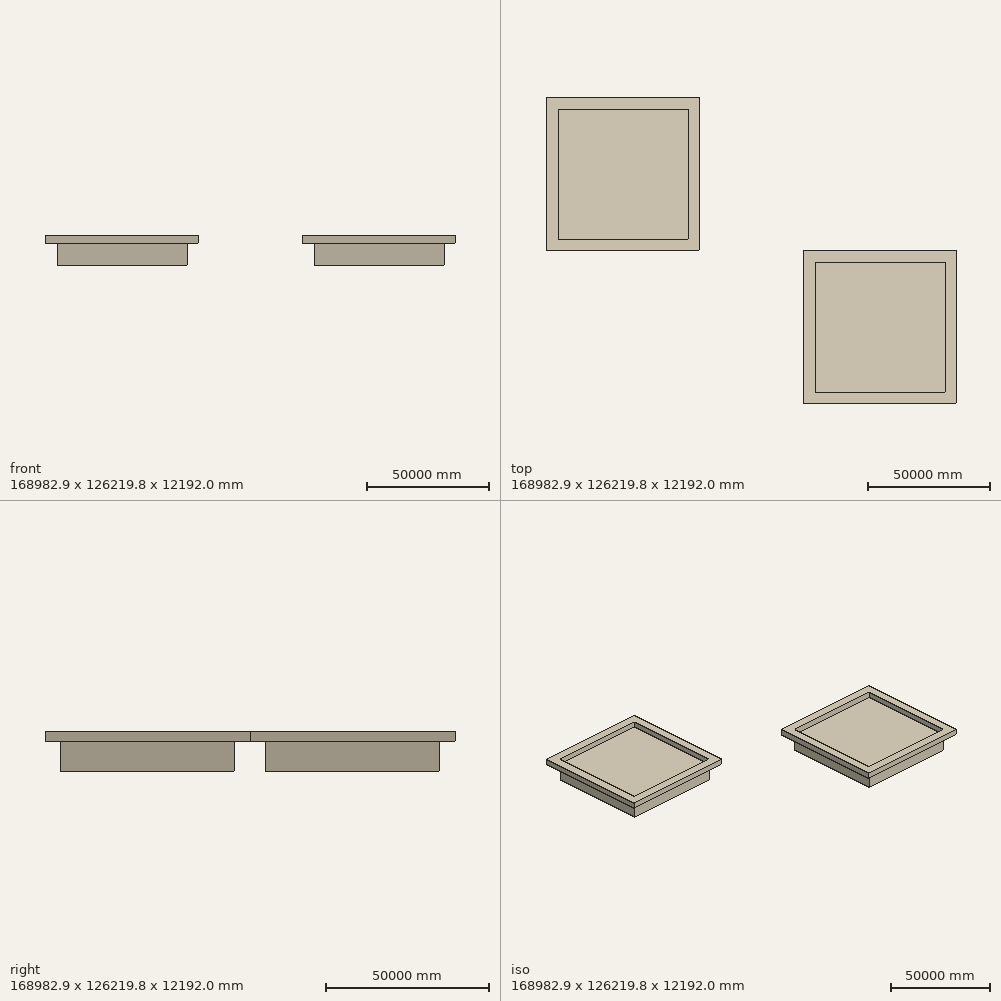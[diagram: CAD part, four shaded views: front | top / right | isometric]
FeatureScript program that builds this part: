
annotation { "Feature Type Name" : "Feature", "Feature Type Description" : "" }
export const myFeature = defineFeature(function(context is Context, id is Id, definition is map)
    precondition{}
    {
        {
            var Q0;
            Q0=qCreatedBy(makeId("Top.planeOp"),FACE);
            var sketch = newSketch(context, id + "F0", { "sketchPlane" : qUnion([Q0])});
            skLineSegment(sketch, "E0.bottom", {"start": v(-63217.3, 63126.24) * mm, "end": v(-123.7, 63126.24) * mm});
            skLineSegment(sketch, "E0.top", {"start": v(-63217.3, 32.64) * mm, "end": v(-123.7, 32.64) * mm});
            skLineSegment(sketch, "E0.left", {"start": v(-63217.3, 63126.24) * mm, "end": v(-63217.3, 32.64) * mm});
            skLineSegment(sketch, "E0.right", {"start": v(-123.7, 63126.24) * mm, "end": v(-123.7, 32.64) * mm});
            skSolve(sketch);
        }
        {
            var Q0;
            Q0=makeQuery(id+"F0.imprint","IMPRINT",FACE,{"disambiguationData":[TD([[makeQuery(id+"F0.imprint","IMPRINT",EDGE,{"derivedFrom":sQuery(id+"F0.wireOp",EDGE,"E0.bottom")}),-1.0]])]});
            var sketch = newSketch(context, id + "F1", { "sketchPlane" : qUnion([Q0])});
            skLineSegment(sketch, "E1.bottom", {"start": v(-58340.5, 58249.44) * mm, "end": v(-4695.7, 58249.44) * mm});
            skLineSegment(sketch, "E1.top", {"start": v(-58340.5, 4604.64) * mm, "end": v(-4695.7, 4604.64) * mm});
            skLineSegment(sketch, "E1.left", {"start": v(-58340.5, 58249.44) * mm, "end": v(-58340.5, 4604.64) * mm});
            skLineSegment(sketch, "E1.right", {"start": v(-4695.7, 58249.44) * mm, "end": v(-4695.7, 4604.64) * mm});
            skLineSegment(sketch, "E2", {"start": v(0, 32710.06) * mm, "end": v(42672, 32710.06) * mm});
            skLineSegment(sketch, "E3", {"start": v(42672, 32710.06) * mm, "end": v(42672, 0) * mm});
            skLineSegment(sketch, "E4.bottom", {"start": v(42672, 0) * mm, "end": v(105765.6, 0) * mm});
            skLineSegment(sketch, "E4.top", {"start": v(42672, -63093.6) * mm, "end": v(105765.6, -63093.6) * mm});
            skLineSegment(sketch, "E4.left", {"start": v(42672, 0) * mm, "end": v(42672, -63093.6) * mm});
            skLineSegment(sketch, "E4.right", {"start": v(105765.6, 0) * mm, "end": v(105765.6, -63093.6) * mm});
            skLineSegment(sketch, "E5.bottom", {"start": v(47548.8, -4876.8) * mm, "end": v(101193.6, -4876.8) * mm});
            skLineSegment(sketch, "E5.top", {"start": v(47548.8, -58521.6) * mm, "end": v(101193.6, -58521.6) * mm});
            skLineSegment(sketch, "E5.left", {"start": v(47548.8, -4876.8) * mm, "end": v(47548.8, -58521.6) * mm});
            skLineSegment(sketch, "E5.right", {"start": v(101193.6, -4876.8) * mm, "end": v(101193.6, -58521.6) * mm});
            skSolve(sketch);
        }
        {
            var Q0;
            Q0=makeQuery(id+"F1.imprint","IMPRINT",FACE,{"disambiguationData":[TD([[makeQuery(id+"F1.imprint","IMPRINT",EDGE,{"derivedFrom":sQuery(id+"F1.wireOp",EDGE,"E1.bottom")}),-1.0]])]});
            var Q1;
            Q1=makeQuery(id+"F1.imprint","IMPRINT",FACE,{"disambiguationData":[TD([[makeQuery(id+"F1.imprint","IMPRINT",EDGE,{"derivedFrom":sQuery(id+"F1.wireOp",EDGE,"E5.bottom")}),-1.0]])]});
            extrude(context, id + "F2", {"entities" : qUnion([Q0, Q1]), "oppositeDirection" : true, "depth" : 9144 * mm, "offsetDistance" : 30.48 * mm});
        }
        {
            var Q0;
            Q0=makeQuery(id+"F1.imprint","IMPRINT",FACE,{"disambiguationData":[TD([[makeQuery(id+"F1.imprint","IMPRINT",EDGE,{"derivedFrom":sQuery(id+"F1.wireOp",EDGE,"E1.bottom")}),1.0]])]});
            var Q1;
            Q1=makeQuery(id+"F0.imprint","IMPRINT",FACE,{"disambiguationData":[TD([[makeQuery(id+"F0.imprint","IMPRINT",EDGE,{"derivedFrom":sQuery(id+"F0.wireOp",EDGE,"WmE8Zd7i-H0mA-me1j-kzmZ-1MaX5TtAPcwQ.bottom")}),-1.0]])]});
            var Q2;
            Q2=makeQuery(id+"F1.imprint","IMPRINT",FACE,{"disambiguationData":[TD([[makeQuery(id+"F1.imprint","IMPRINT",EDGE,{"derivedFrom":sQuery(id+"F1.wireOp",EDGE,"E4.bottom")}),-1.0]])]});
            extrude(context, id + "F3", {"entities" : qUnion([Q0, Q1, Q2]), "depth" : 3048 * mm, "offsetDistance" : 30.48 * mm});
        }
    });
